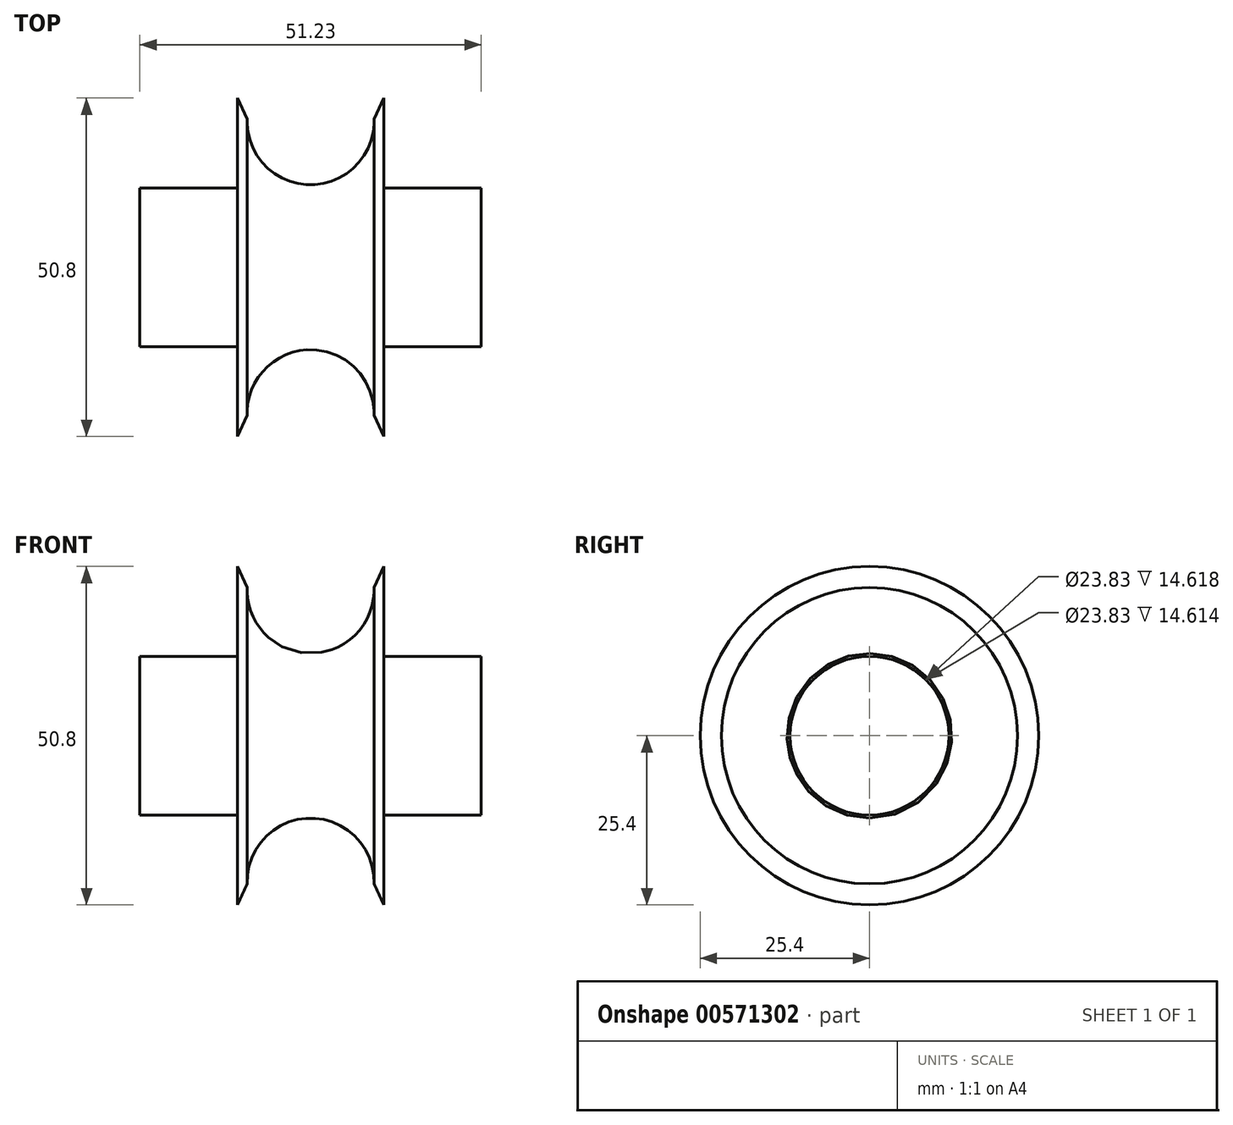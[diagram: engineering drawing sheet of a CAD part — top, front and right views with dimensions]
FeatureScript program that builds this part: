
annotation { "Feature Type Name" : "Feature", "Feature Type Description" : "" }
export const myFeature = defineFeature(function(context is Context, id is Id, definition is map)
    precondition{}
    {
        {
            var Q0;
            Q0=qCreatedBy(makeId("Front.planeOp"),FACE);
            var sketch = newSketch(context, id + "F0", { "sketchPlane" : qUnion([Q0])});
            skLineSegment(sketch, "E0", {"start": v(-12.17, 25.4) * mm, "end": v(-10.7, 22.22) * mm});
            skLineSegment(sketch, "E1", {"start": v(9.83, 25.4) * mm, "end": v(8.35, 22.22) * mm});
            skLineSegment(sketch, "E2", {"start": v(-12.17, 11.91) * mm, "end": v(-26.79, 11.91) * mm});
            skLineSegment(sketch, "E3", {"start": v(-26.79, 11.91) * mm, "end": v(-26.79, 0) * mm});
            skLineSegment(sketch, "E4", {"start": v(9.83, 11.91) * mm, "end": v(24.44, 11.91) * mm});
            skLineSegment(sketch, "E5", {"start": v(24.44, 11.91) * mm, "end": v(24.44, 0) * mm});
            skArc(sketch, "E6", {"start": v(-10.7, 22.22) * mm, "mid": v(-1.17, 12.37) * mm, "end": v(8.35, 22.22) * mm});
            skLineSegment(sketch, "E7", {"start": v(-76.68, 0) * mm, "end": v(76.88, 0) * mm, "construction": true});
            skLineSegment(sketch, "E8", {"start": v(9.83, 25.4) * mm, "end": v(9.83, 11.91) * mm});
            skLineSegment(sketch, "E9", {"start": v(9.83, 11.91) * mm, "end": v(9.83, 0) * mm});
            skLineSegment(sketch, "E10", {"start": v(-12.17, 25.4) * mm, "end": v(-12.17, 11.91) * mm});
            skLineSegment(sketch, "E11", {"start": v(-12.17, 11.91) * mm, "end": v(-12.17, 0) * mm});
            skSolve(sketch);
        }
        {
            var Q0;
            Q0=sQuery(id+"F0.wireOp",EDGE,"E10");
            var Q1;
            Q1=sQuery(id+"F0.wireOp",EDGE,"E0");
            var Q2;
            Q2=sQuery(id+"F0.wireOp",EDGE,"E6");
            var Q3;
            Q3=sQuery(id+"F0.wireOp",EDGE,"E1");
            var Q4;
            Q4=sQuery(id+"F0.wireOp",EDGE,"E4");
            var Q5;
            Q5=sQuery(id+"F0.wireOp",EDGE,"E2");
            var Q6;
            Q6=sQuery(id+"F0.wireOp",EDGE,"E3");
            var Q7;
            Q7=sQuery(id+"F0.wireOp",EDGE,"E5");
            var Q8;
            Q8=sQuery(id+"F0.wireOp",EDGE,"E8");
            var Q9;
            Q9=sQuery(id+"F0.wireOp",EDGE,"E7");
            revolve(context, id + "F1", {"bodyType" : ToolBodyType.SURFACE, "operationType" : NewBodyOperationType.ADD, "surfaceEntities" : qUnion([Q0, Q1, Q2, Q3, Q4, Q5, Q6, Q7, Q8]), "axis" : qUnion([Q9]), "revolveType" : RevolveType.FULL});
        }
    });
